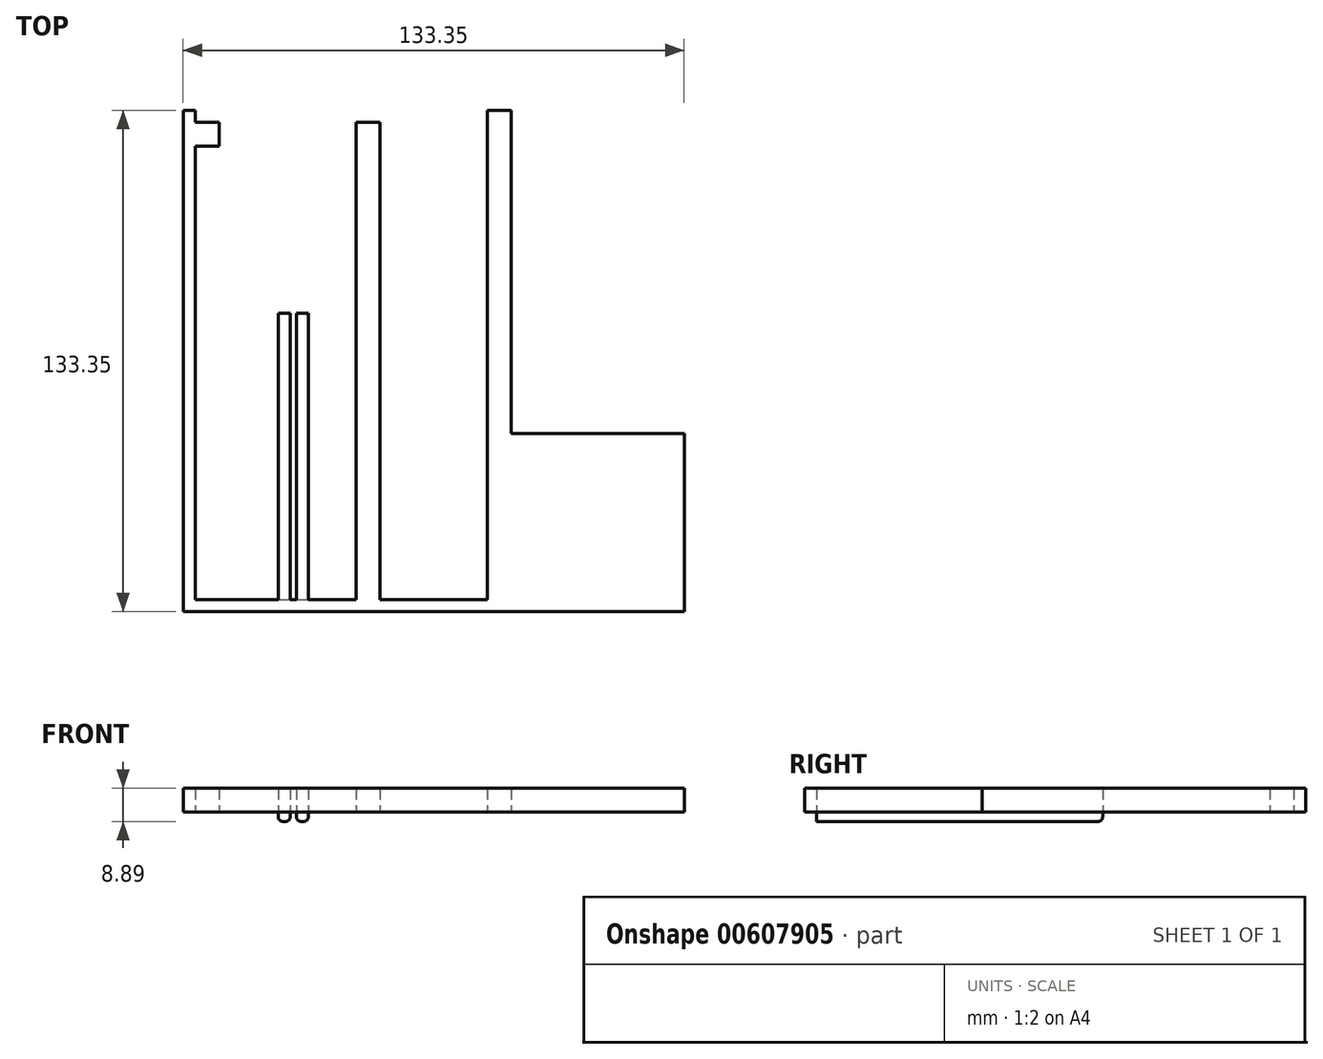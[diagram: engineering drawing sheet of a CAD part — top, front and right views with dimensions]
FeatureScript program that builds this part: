
annotation { "Feature Type Name" : "Feature", "Feature Type Description" : "" }
export const myFeature = defineFeature(function(context is Context, id is Id, definition is map)
    precondition{}
    {
        {
            var Q0;
            Q0=qCreatedBy(makeId("Top.planeOp"),FACE);
            var sketch = newSketch(context, id + "F0", { "sketchPlane" : qUnion([Q0])});
            skLineSegment(sketch, "E0.0", {"start": v(-62.5, 62.83) * mm, "end": v(64.5, 62.83) * mm});
            skLineSegment(sketch, "E0.1", {"start": v(-62.5, 62.83) * mm, "end": v(-62.5, -64.17) * mm});
            skLineSegment(sketch, "E0.2", {"start": v(-62.5, -64.17) * mm, "end": v(64.5, -64.17) * mm});
            skLineSegment(sketch, "E0.3", {"start": v(64.5, 62.83) * mm, "end": v(64.5, -64.17) * mm});
            skLineSegment(sketch, "E1.bottom", {"start": v(1, 62.83) * mm, "end": v(-13.3, 62.83) * mm});
            skLineSegment(sketch, "E1.top", {"start": v(1, -64.17) * mm, "end": v(-13.3, -64.17) * mm});
            skLineSegment(sketch, "E1.right", {"start": v(-13.3, 62.83) * mm, "end": v(-13.3, -64.17) * mm});
            skLineSegment(sketch, "E2.bottom", {"start": v(1, 62.83) * mm, "end": v(15.29, 62.83) * mm});
            skLineSegment(sketch, "E2.top", {"start": v(1, -64.17) * mm, "end": v(15.29, -64.17) * mm});
            skLineSegment(sketch, "E2.right", {"start": v(15.29, 62.83) * mm, "end": v(15.29, -64.17) * mm});
            skLineSegment(sketch, "E3.0", {"start": v(-19.65, 27.9) * mm, "end": v(-19.65, -64.17) * mm});
            skLineSegment(sketch, "E4.0", {"start": v(21.64, 27.9) * mm, "end": v(21.64, -64.17) * mm});
            skLineSegment(sketch, "E5", {"start": v(1, -64.17) * mm, "end": v(1, 62.83) * mm});
            skLineSegment(sketch, "E6", {"start": v(1, -64.17) * mm, "end": v(1, -43.85) * mm});
            skCircle(sketch, "E7", {"center": v(1, -43.85) * mm, "radius": 14.29 * mm});
            skLineSegment(sketch, "E8", {"start": v(1, -29.56) * mm, "end": v(1, -23.21) * mm});
            skLineSegment(sketch, "E9", {"start": v(15.29, -23.21) * mm, "end": v(-13.3, -23.21) * mm});
            skLineSegment(sketch, "E10", {"start": v(-13.3, -23.21) * mm, "end": v(-19.65, -23.21) * mm});
            skLineSegment(sketch, "E11", {"start": v(-62.5, 62.83) * mm, "end": v(-65.68, 62.83) * mm});
            skLineSegment(sketch, "E12", {"start": v(64.5, 62.83) * mm, "end": v(67.67, 62.83) * mm});
            skLineSegment(sketch, "E13", {"start": v(21.64, 27.9) * mm, "end": v(21.64, 62.83) * mm});
            skLineSegment(sketch, "E14", {"start": v(-19.65, 27.9) * mm, "end": v(-19.65, 62.83) * mm});
            skLineSegment(sketch, "E15", {"start": v(21.64, 62.83) * mm, "end": v(21.64, 66) * mm});
            skLineSegment(sketch, "E16", {"start": v(15.29, 62.83) * mm, "end": v(15.29, 66) * mm});
            skLineSegment(sketch, "E17", {"start": v(64.5, -64.17) * mm, "end": v(64.5, -67.35) * mm});
            skLineSegment(sketch, "E18", {"start": v(64.5, -23.21) * mm, "end": v(67.67, -23.21) * mm});
            skLineSegment(sketch, "E19.bottom", {"start": v(32.75, -23.21) * mm, "end": v(15.29, -23.21) * mm});
            skLineSegment(sketch, "E19.top", {"start": v(32.75, -64.17) * mm, "end": v(15.29, -64.17) * mm});
            skLineSegment(sketch, "E19.left", {"start": v(32.75, -23.21) * mm, "end": v(32.75, -64.17) * mm});
            skLineSegment(sketch, "E19.right", {"start": v(15.29, -23.21) * mm, "end": v(15.29, -64.17) * mm});
            skLineSegment(sketch, "E20", {"start": v(32.75, -23.21) * mm, "end": v(64.5, -23.21) * mm});
            skLineSegment(sketch, "E21", {"start": v(64.5, -23.21) * mm, "end": v(64.5, -20.04) * mm});
            skLineSegment(sketch, "E22", {"start": v(64.5, -20.04) * mm, "end": v(21.64, -20.04) * mm});
            skLineSegment(sketch, "E23", {"start": v(32.75, -23.21) * mm, "end": v(32.75, -26.39) * mm});
            skLineSegment(sketch, "E24", {"start": v(32.75, -26.39) * mm, "end": v(64.5, -26.39) * mm});
            skLineSegment(sketch, "E25.bottom", {"start": v(15.29, 62.83) * mm, "end": v(8.94, 62.83) * mm});
            skLineSegment(sketch, "E25.top", {"start": v(15.29, 56.48) * mm, "end": v(8.94, 56.48) * mm});
            skLineSegment(sketch, "E25.left", {"start": v(15.29, 62.83) * mm, "end": v(15.29, 56.48) * mm});
            skLineSegment(sketch, "E25.right", {"start": v(8.94, 62.83) * mm, "end": v(8.94, 56.48) * mm});
            skLineSegment(sketch, "E26.bottom", {"start": v(-62.5, 62.83) * mm, "end": v(-56.15, 62.83) * mm});
            skLineSegment(sketch, "E26.top", {"start": v(-62.5, 56.48) * mm, "end": v(-56.15, 56.48) * mm});
            skLineSegment(sketch, "E26.left", {"start": v(-62.5, 62.83) * mm, "end": v(-62.5, 56.48) * mm});
            skLineSegment(sketch, "E26.right", {"start": v(-56.15, 62.83) * mm, "end": v(-56.15, 56.48) * mm});
            skLineSegment(sketch, "E27", {"start": v(-62.5, 62.83) * mm, "end": v(-62.5, 66) * mm});
            skLineSegment(sketch, "E28", {"start": v(-19.65, -64.17) * mm, "end": v(-35.53, -64.17) * mm});
            skLineSegment(sketch, "E29", {"start": v(-35.53, -64.17) * mm, "end": v(-35.53, 12.03) * mm});
            skLineSegment(sketch, "E30", {"start": v(-35.53, 12.03) * mm, "end": v(-32.35, 12.03) * mm});
            skLineSegment(sketch, "E31", {"start": v(-32.35, 12.03) * mm, "end": v(-32.35, -64.17) * mm});
            skLineSegment(sketch, "E32", {"start": v(-35.53, -64.17) * mm, "end": v(-40.85, -64.17) * mm});
            skLineSegment(sketch, "E33", {"start": v(-35.53, -64.17) * mm, "end": v(-37.2, -64.17) * mm});
            skLineSegment(sketch, "E34", {"start": v(-37.2, -64.17) * mm, "end": v(-37.2, 12.03) * mm});
            skLineSegment(sketch, "E35", {"start": v(-37.2, 12.03) * mm, "end": v(-40.37, 12.03) * mm});
            skLineSegment(sketch, "E36", {"start": v(-40.37, 12.03) * mm, "end": v(-40.37, -64.17) * mm});
            skLineSegment(sketch, "E37", {"start": v(64.5, -20.04) * mm, "end": v(67.67, -20.04) * mm});
            skLineSegment(sketch, "E38.bottom", {"start": v(-65.68, 66) * mm, "end": v(67.67, 66) * mm});
            skLineSegment(sketch, "E38.top", {"start": v(-65.68, -67.35) * mm, "end": v(67.67, -67.35) * mm});
            skLineSegment(sketch, "E38.left", {"start": v(-65.68, 66) * mm, "end": v(-65.68, -67.35) * mm});
            skLineSegment(sketch, "E38.right", {"start": v(67.67, 66) * mm, "end": v(67.67, -67.35) * mm});
            skSolve(sketch);
        }
        {
            var Q0;
            {var subQ0=sQuery(id+"F0.wireOp",EDGE,"E29");Q0=makeQuery(id+"F0.imprint","IMPRINT",FACE,{"disambiguationData":[TD([[makeQuery(id+"F0.imprint","IMPRINT",EDGE,{"derivedFrom":subQ0}),-1.0]])]});}
            var Q1;
            {var subQ0=sQuery(id+"F0.wireOp",EDGE,"E34");Q1=makeQuery(id+"F0.imprint","IMPRINT",FACE,{"disambiguationData":[TD([[makeQuery(id+"F0.imprint","IMPRINT",EDGE,{"derivedFrom":subQ0}),1.0]])]});}
            extrude(context, id + "F1", {"entities" : qUnion([Q0, Q1]), "oppositeDirection" : true, "depth" : 2.54 * mm, "offsetDistance" : 25.4 * mm});
        }
        {
            var Q0;
            {var subQ12=sQuery(id+"F0.wireOp",EDGE,"E0.1");Q0=makeQuery(id+"F0.imprint","IMPRINT",FACE,{"disambiguationData":[TD([[makeQuery(id+"F0.imprint","IMPRINT",EDGE,{"derivedFrom":subQ12}),1.0]])]});}
            var Q1;
            {var subQ10=sQuery(id+"F0.wireOp",EDGE,"E0.1");Q1=makeQuery(id+"F0.imprint","IMPRINT",FACE,{"disambiguationData":[TD([[makeQuery(id+"F0.imprint","IMPRINT",EDGE,{"derivedFrom":subQ10}),-1.0]])]});}
            var Q2;
            {var subQ5=sQuery(id+"F0.wireOp",EDGE,"E10");Q2=makeQuery(id+"F0.imprint","IMPRINT",FACE,{"disambiguationData":[TD([[makeQuery(id+"F0.imprint","IMPRINT",EDGE,{"derivedFrom":subQ5}),1.0]])]});}
            var Q3;
            {var subQ5=sQuery(id+"F0.wireOp",EDGE,"E1.top");Q3=makeQuery(id+"F0.imprint","IMPRINT",FACE,{"disambiguationData":[TD([[makeQuery(id+"F0.imprint","IMPRINT",EDGE,{"derivedFrom":subQ5}),-1.0]])]});}
            var Q4;
            {var subQ0=sQuery(id+"F0.wireOp",EDGE,"E8");Q4=makeQuery(id+"F0.imprint","IMPRINT",FACE,{"disambiguationData":[TD([[makeQuery(id+"F0.imprint","IMPRINT",EDGE,{"derivedFrom":subQ0}),-1.0]])]});}
            var Q5;
            {var subQ0=sQuery(id+"F0.wireOp",EDGE,"E2.top");Q5=makeQuery(id+"F0.imprint","IMPRINT",FACE,{"disambiguationData":[TD([[makeQuery(id+"F0.imprint","IMPRINT",EDGE,{"derivedFrom":subQ0}),1.0]])]});}
            var Q6;
            {var subQ1=sQuery(id+"F0.wireOp",EDGE,"E19.top");var subQ3=sQuery(id+"F0.wireOp",EDGE,"E4.0");var subQ4=makeQuery(id+"F0.imprint","INTERSECT",VERTEX,{"derivedFrom":[subQ3,subQ1]});Q6=makeQuery(id+"F0.imprint","IMPRINT",FACE,{"disambiguationData":[TD([[makeQuery(id+"F0.imprint","IMPRINT",EDGE,{"disambiguationData":[TD([[subQ4,1.0]])],"derivedFrom":subQ3}),-1.0]])]});}
            var Q7;
            {var subQ0=sQuery(id+"F0.wireOp",EDGE,"E19.left");Q7=makeQuery(id+"F0.imprint","IMPRINT",FACE,{"disambiguationData":[TD([[makeQuery(id+"F0.imprint","IMPRINT",EDGE,{"derivedFrom":subQ0}),-1.0]])]});}
            var Q8;
            {var subQ3=sQuery(id+"F0.wireOp",EDGE,"E19.left");Q8=makeQuery(id+"F0.imprint","IMPRINT",FACE,{"disambiguationData":[TD([[makeQuery(id+"F0.imprint","IMPRINT",EDGE,{"derivedFrom":subQ3}),1.0]])]});}
            var Q9;
            {var subQ0=sQuery(id+"F0.wireOp",EDGE,"E20");Q9=makeQuery(id+"F0.imprint","IMPRINT",FACE,{"disambiguationData":[TD([[makeQuery(id+"F0.imprint","IMPRINT",EDGE,{"derivedFrom":subQ0}),-1.0]])]});}
            var Q10;
            {var subQ0=sQuery(id+"F0.wireOp",EDGE,"E20");Q10=makeQuery(id+"F0.imprint","IMPRINT",FACE,{"disambiguationData":[TD([[makeQuery(id+"F0.imprint","IMPRINT",EDGE,{"derivedFrom":subQ0}),1.0]])]});}
            var Q11;
            {var subQ1=sQuery(id+"F0.wireOp",EDGE,"E17");Q11=makeQuery(id+"F0.imprint","IMPRINT",FACE,{"disambiguationData":[TD([[makeQuery(id+"F0.imprint","IMPRINT",EDGE,{"derivedFrom":subQ1}),1.0]])]});}
            var Q12;
            {var subQ4=sQuery(id+"F0.wireOp",EDGE,"E2.bottom");Q12=makeQuery(id+"F0.imprint","IMPRINT",FACE,{"disambiguationData":[TD([[makeQuery(id+"F0.imprint","IMPRINT",EDGE,{"derivedFrom":subQ4}),-1.0]])]});}
            var Q13;
            {var subQ0=sQuery(id+"F0.wireOp",EDGE,"E10");Q13=makeQuery(id+"F0.imprint","IMPRINT",FACE,{"disambiguationData":[TD([[makeQuery(id+"F0.imprint","IMPRINT",EDGE,{"derivedFrom":subQ0}),-1.0]])]});}
            var Q14;
            {var subQ0=sQuery(id+"F0.wireOp",EDGE,"E1.bottom");Q14=makeQuery(id+"F0.imprint","IMPRINT",FACE,{"disambiguationData":[TD([[makeQuery(id+"F0.imprint","IMPRINT",EDGE,{"derivedFrom":subQ0}),1.0]])]});}
            var Q15;
            {var subQ0=sQuery(id+"F0.wireOp",EDGE,"E1.bottom");Q15=makeQuery(id+"F0.imprint","IMPRINT",FACE,{"disambiguationData":[TD([[makeQuery(id+"F0.imprint","IMPRINT",EDGE,{"derivedFrom":subQ0}),-1.0]])]});}
            var Q16;
            Q16=makeQuery(id+"F0.imprint","IMPRINT",FACE,{"disambiguationData":[TD([[makeQuery(id+"F0.imprint","IMPRINT",EDGE,{"derivedFrom":sQuery(id+"F0.wireOp",EDGE,"E26.bottom")}),-1.0]])]});
            var Q17;
            {var subQ0=sQuery(id+"F0.wireOp",EDGE,"E11");Q17=makeQuery(id+"F0.imprint","IMPRINT",FACE,{"disambiguationData":[TD([[makeQuery(id+"F0.imprint","IMPRINT",EDGE,{"derivedFrom":subQ0}),-1.0]])]});}
            var Q18;
            Q18=makeQuery(id+"F0.imprint","IMPRINT",FACE,{"disambiguationData":[TD([[makeQuery(id+"F0.imprint","IMPRINT",EDGE,{"derivedFrom":sQuery(id+"F0.wireOp",EDGE,"E25.bottom")}),1.0]])]});
            var Q19;
            {var subQ4=sQuery(id+"F0.wireOp",EDGE,"E2.right");Q19=makeQuery(id+"F0.imprint","IMPRINT",FACE,{"disambiguationData":[TD([[makeQuery(id+"F0.imprint","IMPRINT",EDGE,{"derivedFrom":subQ4}),1.0]])]});}
            var Q20;
            {var subQ0=sQuery(id+"F0.wireOp",EDGE,"E15");Q20=makeQuery(id+"F0.imprint","IMPRINT",FACE,{"disambiguationData":[TD([[makeQuery(id+"F0.imprint","IMPRINT",EDGE,{"derivedFrom":subQ0}),1.0]])]});}
            var Q21;
            {var subQ0=sQuery(id+"F0.wireOp",EDGE,"E18");Q21=makeQuery(id+"F0.imprint","IMPRINT",FACE,{"disambiguationData":[TD([[makeQuery(id+"F0.imprint","IMPRINT",EDGE,{"derivedFrom":subQ0}),1.0]])]});}
            var Q22;
            {var subQ0=sQuery(id+"F0.wireOp",EDGE,"E29");Q22=makeQuery(id+"F0.imprint","IMPRINT",FACE,{"disambiguationData":[TD([[makeQuery(id+"F0.imprint","IMPRINT",EDGE,{"derivedFrom":subQ0}),-1.0]])]});}
            var Q23;
            {var subQ0=sQuery(id+"F0.wireOp",EDGE,"E34");Q23=makeQuery(id+"F0.imprint","IMPRINT",FACE,{"disambiguationData":[TD([[makeQuery(id+"F0.imprint","IMPRINT",EDGE,{"derivedFrom":subQ0}),1.0]])]});}
            extrude(context, id + "F2", {"entities" : qUnion([Q0, Q1, Q2, Q3, Q4, Q5, Q6, Q7, Q8, Q9, Q10, Q11, Q12, Q13, Q14, Q15, Q16, Q17, Q18, Q19, Q20, Q21, Q22, Q23]), "depth" : 6.35 * mm, "offsetDistance" : 25.4 * mm});
        }
        {
            var Q0;
            Q0=makeQuery(id+"F1.opExtrude","CAP_EDGE",EDGE,{"disambiguationData":[OSD([sQuery(id+"F0.wireOp",EDGE,"E36")])],"isStart":false});
            var Q1;
            Q1=makeQuery(id+"F1.opExtrude","CAP_EDGE",EDGE,{"disambiguationData":[OSD([sQuery(id+"F0.wireOp",EDGE,"E35")])],"isStart":false});
            var Q2;
            Q2=makeQuery(id+"F1.opExtrude","SWEPT_EDGE",EDGE,{"disambiguationData":[OSD([sQuery(id+"F0.wireOp",EDGE,"E35"),sQuery(id+"F0.wireOp",EDGE,"E36")])]});
            var Q3;
            Q3=makeQuery(id+"F1.opExtrude","CAP_EDGE",EDGE,{"disambiguationData":[OSD([sQuery(id+"F0.wireOp",EDGE,"E34")])],"isStart":false});
            var Q4;
            Q4=makeQuery(id+"F1.opExtrude","CAP_EDGE",EDGE,{"disambiguationData":[OSD([sQuery(id+"F0.wireOp",EDGE,"E29")])],"isStart":false});
            var Q5;
            Q5=makeQuery(id+"F1.opExtrude","SWEPT_EDGE",EDGE,{"disambiguationData":[OSD([sQuery(id+"F0.wireOp",EDGE,"E34"),sQuery(id+"F0.wireOp",EDGE,"E35")])]});
            var Q6;
            Q6=makeQuery(id+"F1.opExtrude","SWEPT_EDGE",EDGE,{"disambiguationData":[OSD([sQuery(id+"F0.wireOp",EDGE,"E29"),sQuery(id+"F0.wireOp",EDGE,"E30")])]});
            var Q7;
            Q7=makeQuery(id+"F1.opExtrude","CAP_EDGE",EDGE,{"disambiguationData":[OSD([sQuery(id+"F0.wireOp",EDGE,"E30")])],"isStart":false});
            var Q8;
            Q8=makeQuery(id+"F1.opExtrude","SWEPT_EDGE",EDGE,{"disambiguationData":[OSD([sQuery(id+"F0.wireOp",EDGE,"E30"),sQuery(id+"F0.wireOp",EDGE,"E31")])]});
            var Q9;
            Q9=makeQuery(id+"F1.opExtrude","CAP_EDGE",EDGE,{"disambiguationData":[OSD([sQuery(id+"F0.wireOp",EDGE,"E31")])],"isStart":false});
            fillet(context, id + "F3", {"entities" : qUnion([Q0, Q1, Q2, Q3, Q4, Q5, Q6, Q7, Q8, Q9]), "radius" : 1.27 * mm, "tangentPropagation" : true, "allowEdgeOverflow" : false});
        }
    });
